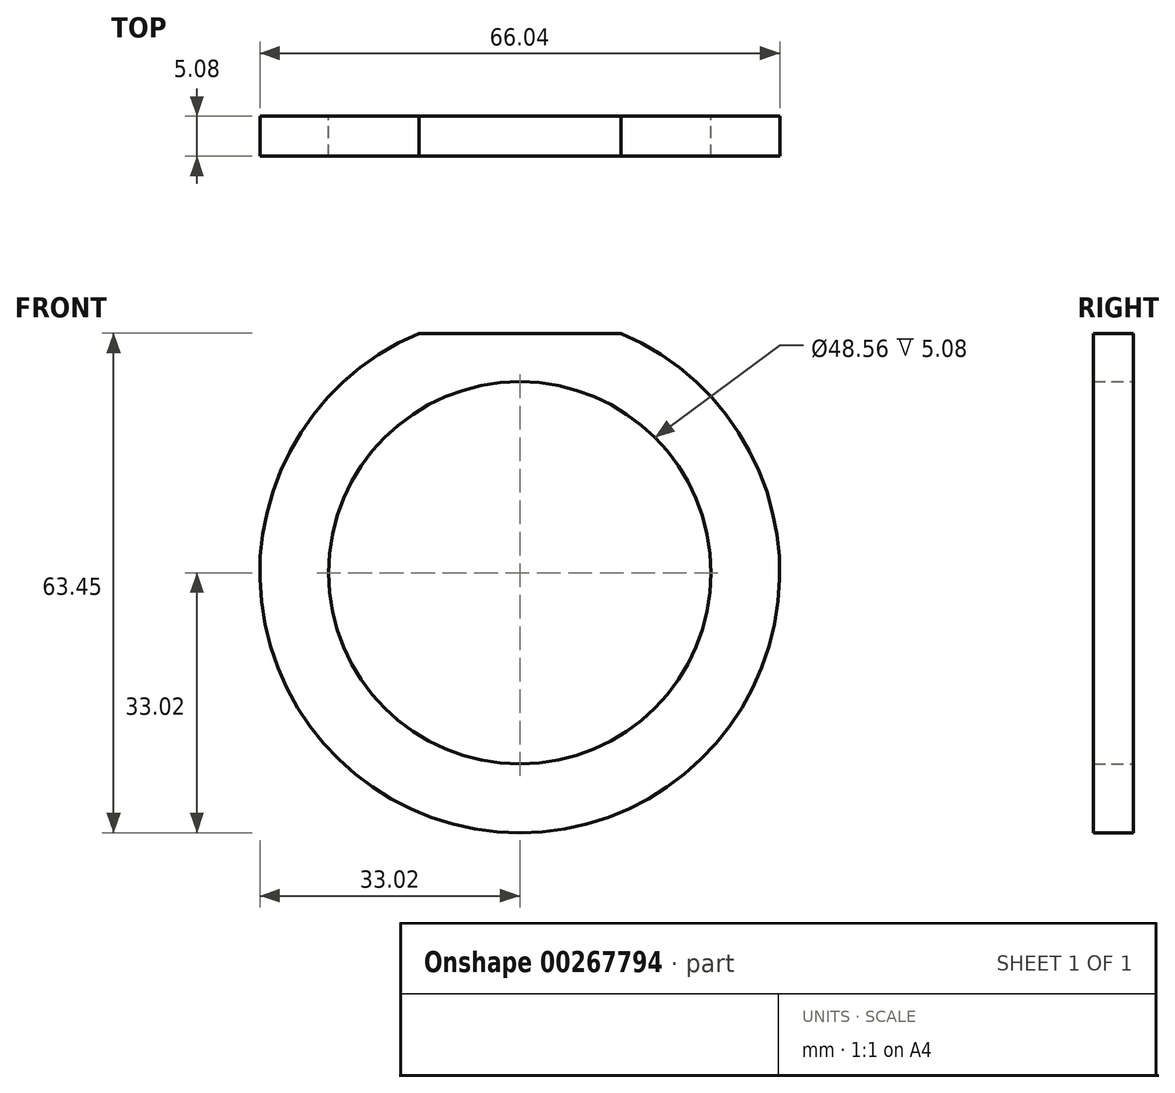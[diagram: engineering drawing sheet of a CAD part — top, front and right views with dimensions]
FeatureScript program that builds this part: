
annotation { "Feature Type Name" : "Feature", "Feature Type Description" : "" }
export const myFeature = defineFeature(function(context is Context, id is Id, definition is map)
    precondition{}
    {
        {
            var Q0;
            Q0=qCreatedBy(makeId("Front.planeOp"),FACE);
            var sketch = newSketch(context, id + "F0", { "sketchPlane" : qUnion([Q0])});
            skCircle(sketch, "E0", {"center": v(0, 0) * mm, "radius": 33.02 * mm});
            skLineSegment(sketch, "E1", {"start": v(-12.83, 30.43) * mm, "end": v(12.83, 30.43) * mm});
            skCircle(sketch, "E2", {"center": v(0, 0) * mm, "radius": 24.28 * mm});
            skSolve(sketch);
        }
        {
            var Q0;
            {var subQ0=sQuery(id+"F0.wireOp",EDGE,"E1");Q0=makeQuery(id+"F0.imprint","IMPRINT",FACE,{"disambiguationData":[TD([[makeQuery(id+"F0.imprint","IMPRINT",EDGE,{"derivedFrom":subQ0}),-1.0]])]});}
            extrude(context, id + "F1", {"entities" : qUnion([Q0]), "depth" : 5.08 * mm});
        }
    });
